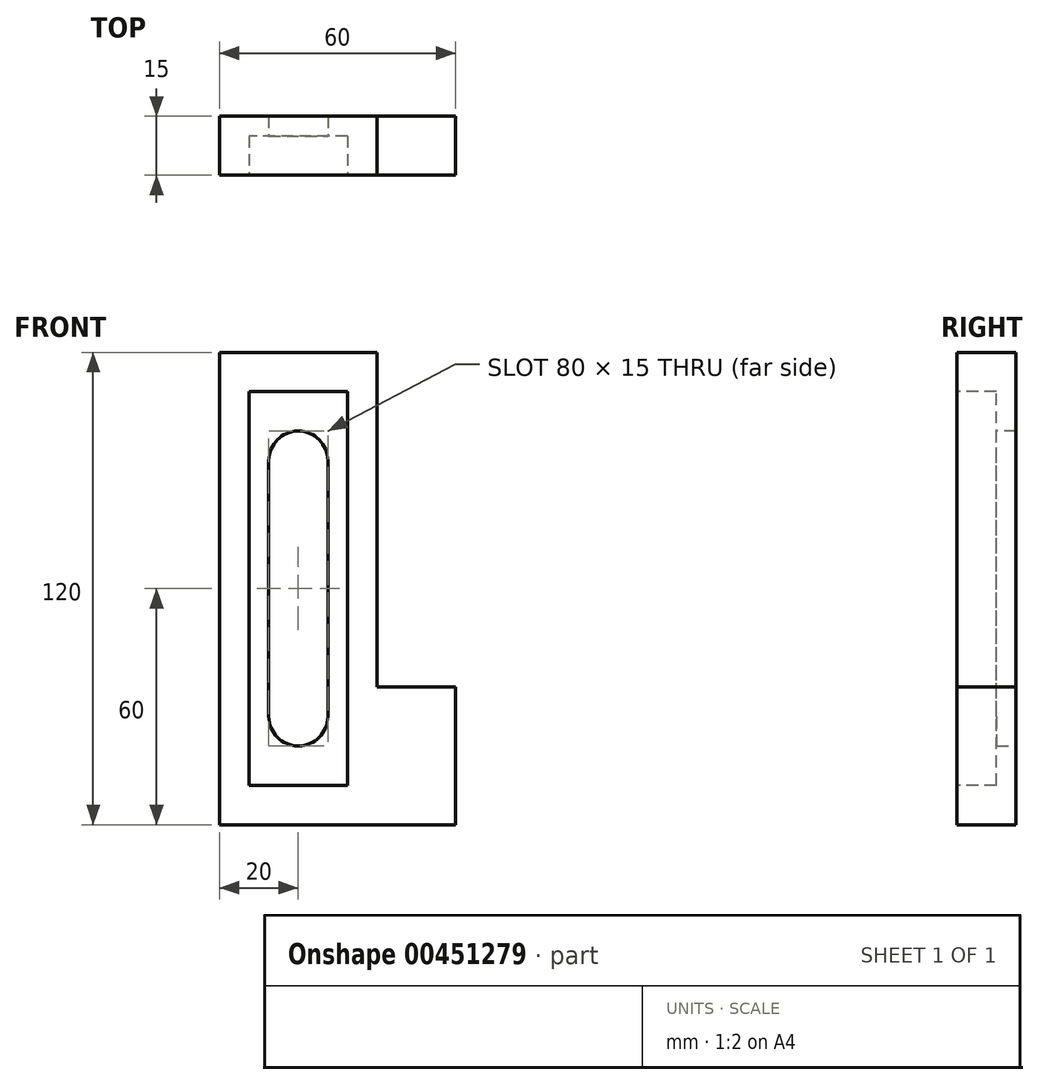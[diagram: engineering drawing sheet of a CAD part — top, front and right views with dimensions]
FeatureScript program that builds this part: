
annotation { "Feature Type Name" : "Feature", "Feature Type Description" : "" }
export const myFeature = defineFeature(function(context is Context, id is Id, definition is map)
    precondition{}
    {
        {
            var Q0;
            Q0=qCreatedBy(makeId("Front.planeOp"),FACE);
            var sketch = newSketch(context, id + "F0", { "sketchPlane" : qUnion([Q0])});
            skLineSegment(sketch, "E0.bottom", {"start": v(12.5, -50) * mm, "end": v(-12.5, -50) * mm});
            skLineSegment(sketch, "E0.top", {"start": v(12.5, 50) * mm, "end": v(-12.5, 50) * mm});
            skLineSegment(sketch, "E0.left", {"start": v(12.5, -50) * mm, "end": v(12.5, 50) * mm});
            skLineSegment(sketch, "E0.right", {"start": v(-12.5, -50) * mm, "end": v(-12.5, 50) * mm});
            skPoint(sketch, "E0.middle", {"position": v(0, 0) * mm});
            skLineSegment(sketch, "E1.bottom", {"start": v(7.5, -40) * mm, "end": v(-7.5, -40) * mm});
            skLineSegment(sketch, "E1.top", {"start": v(7.5, 40) * mm, "end": v(-7.5, 40) * mm});
            skLineSegment(sketch, "E1.left", {"start": v(7.5, -40) * mm, "end": v(7.5, 40) * mm});
            skLineSegment(sketch, "E1.right", {"start": v(-7.5, -40) * mm, "end": v(-7.5, 40) * mm});
            skLineSegment(sketch, "E2.top", {"start": v(20, 60) * mm, "end": v(-20, 60) * mm});
            skLineSegment(sketch, "E2.left", {"start": v(20, -25) * mm, "end": v(20, 60) * mm});
            skLineSegment(sketch, "E2.right", {"start": v(-20, -60) * mm, "end": v(-20, 60) * mm});
            skLineSegment(sketch, "E3", {"start": v(20, -25) * mm, "end": v(40, -25) * mm});
            skLineSegment(sketch, "E4", {"start": v(40, -25) * mm, "end": v(40, -60) * mm});
            skLineSegment(sketch, "E5", {"start": v(-20, -60) * mm, "end": v(40, -60) * mm});
            skPoint(sketch, "E6.orphan", {"position": v(20, -60) * mm});
            skSolve(sketch);
        }
        {
            var Q0;
            Q0=makeQuery(id+"F0.imprint","IMPRINT",FACE,{"disambiguationData":[TD([[makeQuery(id+"F0.imprint","IMPRINT",EDGE,{"derivedFrom":sQuery(id+"F0.wireOp",EDGE,"E0.bottom")}),1.0]])]});
            var Q1;
            Q1=makeQuery(id+"F0.imprint","IMPRINT",FACE,{"disambiguationData":[TD([[makeQuery(id+"F0.imprint","IMPRINT",EDGE,{"derivedFrom":sQuery(id+"F0.wireOp",EDGE,"E0.bottom")}),-1.0]])]});
            var Q2;
            Q2=makeQuery(id+"F0.imprint","IMPRINT",FACE,{"disambiguationData":[TD([[makeQuery(id+"F0.imprint","IMPRINT",EDGE,{"derivedFrom":sQuery(id+"F0.wireOp",EDGE,"E1.bottom")}),-1.0]])]});
            extrude(context, id + "F1", {"entities" : qUnion([Q0, Q1, Q2]), "oppositeDirection" : true, "depth" : 15 * mm});
        }
        {
            var Q0;
            Q0=makeQuery(id+"F0.imprint","IMPRINT",FACE,{"disambiguationData":[TD([[makeQuery(id+"F0.imprint","IMPRINT",EDGE,{"derivedFrom":sQuery(id+"F0.wireOp",EDGE,"E0.bottom")}),-1.0]])]});
            extrude(context, id + "F2", {"entities" : qUnion([Q0]), "operationType" : NewBodyOperationType.REMOVE, "oppositeDirection" : true, "depth" : 10 * mm});
        }
        {
            var Q0;
            Q0=makeQuery(id+"F0.imprint","IMPRINT",FACE,{"disambiguationData":[TD([[makeQuery(id+"F0.imprint","IMPRINT",EDGE,{"derivedFrom":sQuery(id+"F0.wireOp",EDGE,"E1.bottom")}),-1.0]])]});
            extrude(context, id + "F3", {"entities" : qUnion([Q0]), "operationType" : NewBodyOperationType.REMOVE, "endBound" : BoundingType.THROUGH_ALL, "oppositeDirection" : true, "depth" : 25 * mm});
        }
        {
            var Q0;
            Q0=makeQuery(id+"F3.boolean.opBoolean","COPY",EDGE,{"derivedFrom":makeQuery(id+"F3.opExtrude","SWEPT_EDGE",EDGE,{"disambiguationData":[OSD([sQuery(id+"F0.wireOp",EDGE,"E1.top"),sQuery(id+"F0.wireOp",EDGE,"E1.right")])]})});
            var Q1;
            Q1=makeQuery(id+"F3.boolean.opBoolean","COPY",EDGE,{"derivedFrom":makeQuery(id+"F3.opExtrude","SWEPT_EDGE",EDGE,{"disambiguationData":[OSD([sQuery(id+"F0.wireOp",EDGE,"E1.top"),sQuery(id+"F0.wireOp",EDGE,"E1.left")])]})});
            var Q2;
            Q2=makeQuery(id+"F3.boolean.opBoolean","COPY",EDGE,{"derivedFrom":makeQuery(id+"F3.opExtrude","SWEPT_EDGE",EDGE,{"disambiguationData":[OSD([sQuery(id+"F0.wireOp",EDGE,"E1.bottom"),sQuery(id+"F0.wireOp",EDGE,"E1.right")])]})});
            var Q3;
            Q3=makeQuery(id+"F3.boolean.opBoolean","COPY",EDGE,{"derivedFrom":makeQuery(id+"F3.opExtrude","SWEPT_EDGE",EDGE,{"disambiguationData":[OSD([sQuery(id+"F0.wireOp",EDGE,"E1.bottom"),sQuery(id+"F0.wireOp",EDGE,"E1.left")])]})});
            fillet(context, id + "F4", {"entities" : qUnion([Q0, Q1, Q2, Q3]), "radius" : 7.5 * mm, "tangentPropagation" : true, "allowEdgeOverflow" : false});
        }
    });
